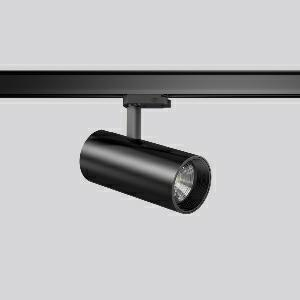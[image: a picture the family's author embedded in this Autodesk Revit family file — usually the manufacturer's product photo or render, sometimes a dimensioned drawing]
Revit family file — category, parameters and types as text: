
# Revit family: deecos_s_mini_742199_003_c0e0
name_source: partatom
category: Lighting Fixtures
units: mm (PartAtom-declared; Revit-internal decimal feet)

## family parameters
Cut with Voids When Loaded = No
Host = Face
Light Source = No
Part Type = Normal
Room Calculation Point = No
Round Connector Dimension = Use Diameter
Shared = No

## types (1)
- DEECOS S mini (1 x LED Modul 930, 2100 lm, 3000)
    Apparent Load = 20 VA
    Approval mark = CE
    CIE Flux Codes = 96 100 100 100 100
    Color Rendering = 90
    Color Temperature = 3000
    Default Elevation = 1800 mm
    Description = Series: DEECOS S mini
LED surface-mounted projector in modern design with no visible cooling ribs. Housing: die-cast aluminium, powder-coated. Rotation range: 356°. Swivel range: 90°. Black plastic ring and recessed LED to prevent glare from the side. Optical assembly with lens made of plastic (polycarbonate) for the best homogeneous light distribution - can be changed without tools. Best colour rendering index Ra>90. With multi adaptor for 3-circuit tracks 230 V. Suitable for Track on ceiling, Wall track. High quality converter without flickering and stroboscopic effect. The following accessories can be mounted without use of tools: interchangeable lenses, decorative glasses, honeycomb louvre, clear and frosted diffusers, white interchangeable plastic ring. 
Colour: deep black, matt (RAL 9005)
Diameter: 87 mm
Height: 214 mm
Lamp: LED
Socket: without socket
Colour temperature: 3000K
Colour rendering index (CRI): 92
System power: 20 W
Rated luminous flux: 2100 lm
Luminous efficiency: 105 lm/W
Control gear: Regulated power supply
Protection class: I
Type of protection: IP 20
    Height = 214 mm
    Lamp = 1 x LED Modul 930
    Lamp Light Flux = 2100 lm
    Lamp count = 1
    Length = 87 mm
    Lifetime = 50000 h
    Luminous efficacy = 105 lm/W
    Manufacturer = RZB
    ModVariant = No
    Model = 742199.003
    Mounting Place = Ceiling
    Mounting Type = Rail mounted
    Number of Poles = 1
    OnlyDefault = Yes
    Power Factor = 1
    Product Name = DEECOS S mini
    Product group = Track mounted projectors
    ProductGroupID = 301
    Protection Class = Protection class I
    Protection Degree = IP 20
    RLX_Detail_Level = 1
    RLX_Emergency_Light_Flux = 0 lm
    RLX_Emergency_Type = 0
    RLX_Emergency_Type_DB = No
    RlxData = <blob elided: 38681 chars, md5=e9988277>
    Socket = socket
    Standby Power = 0 W
    System Light Flux = 2100 lm
    System Power = 20 W
    Type Comments = Product without accessories
    Type Image = 741930.003.jpg
    URL = http://relux.com
    VarID = ---
    Voltage = 230 V
    Voltage Range = 220-240 V
    Weight = 0.00 kg
    Width = 0 mm  [stored 0 ft]

note: [stored X ft] marks values corroborated as IEEE doubles in the binary element streams (Revit-internal decimal feet)

## geometry (parser evidence)
native form markers: Blend x4, Sweep x13
no freeform markers — native parametric forms only
